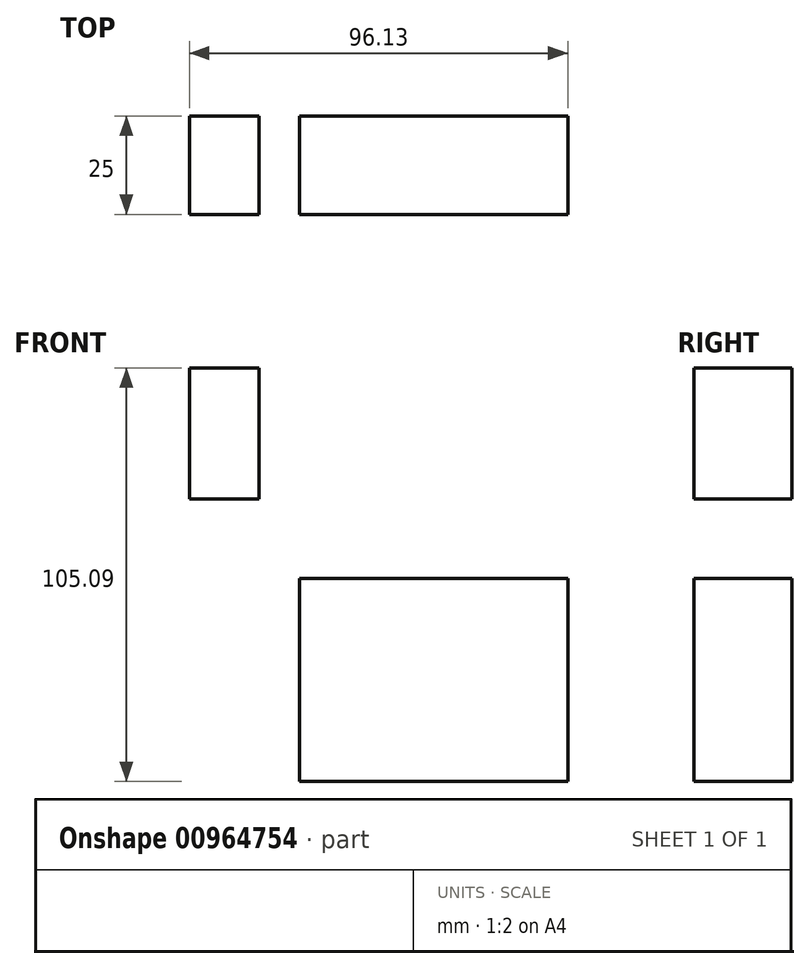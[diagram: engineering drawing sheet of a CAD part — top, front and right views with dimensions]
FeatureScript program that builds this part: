
annotation { "Feature Type Name" : "Feature", "Feature Type Description" : "" }
export const myFeature = defineFeature(function(context is Context, id is Id, definition is map)
    precondition{}
    {
        {
            var Q0;
            Q0=qCreatedBy(makeId("Front.planeOp"),FACE);
            var sketch = newSketch(context, id + "F0", { "sketchPlane" : qUnion([Q0])});
            skLineSegment(sketch, "E0.bottom", {"start": v(-142.36, 53.53) * mm, "end": v(-124.67, 53.53) * mm});
            skLineSegment(sketch, "E0.top", {"start": v(-142.36, 20.25) * mm, "end": v(-124.67, 20.25) * mm});
            skLineSegment(sketch, "E0.left", {"start": v(-142.36, 53.53) * mm, "end": v(-142.36, 20.25) * mm});
            skLineSegment(sketch, "E0.right", {"start": v(-124.67, 53.53) * mm, "end": v(-124.67, 20.25) * mm});
            skLineSegment(sketch, "E1.bottom", {"start": v(-114.32, 0) * mm, "end": v(-46.23, 0) * mm});
            skLineSegment(sketch, "E1.top", {"start": v(-114.32, -51.56) * mm, "end": v(-46.23, -51.56) * mm});
            skLineSegment(sketch, "E1.left", {"start": v(-114.32, 0) * mm, "end": v(-114.32, -51.56) * mm});
            skLineSegment(sketch, "E1.right", {"start": v(-46.23, 0) * mm, "end": v(-46.23, -51.56) * mm});
            skSolve(sketch);
        }
        {
            var Q0;
            Q0 = qSketchRegion(id + "F0", true);
            extrude(context, id + "F1", {"entities" : qUnion([Q0]), "depth" : 25 * mm, "offsetDistance" : 25 * mm});
        }
    });
